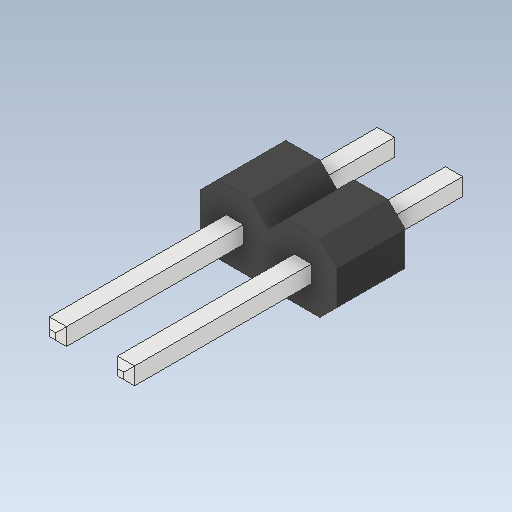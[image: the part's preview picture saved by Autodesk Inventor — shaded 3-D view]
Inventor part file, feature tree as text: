
AUTODESK INVENTOR PART (.ipt)
format: ipt  version: 2020 (Build 240168000, 168)  size: 119,808 bytes
history: imported  units: in
note: dims shown in document units (in); Inventor stores cm internally (conversion verified against a paired STEP export)
features: imported_body x1
ambient origin geometry x8: Origin, YZ Plane, XZ Plane, XY Plane, X Axis, Y Axis, Z Axis, Center Point
bodies: Solid1 (imported_parasolid), Body2 (imported_parasolid)
feature tree (1):
  imported_body  NMx_Import_Brep_tag  [imported B-rep: ~52 faces, bbox_mm=[5.08, 2.54, 12.64]]
